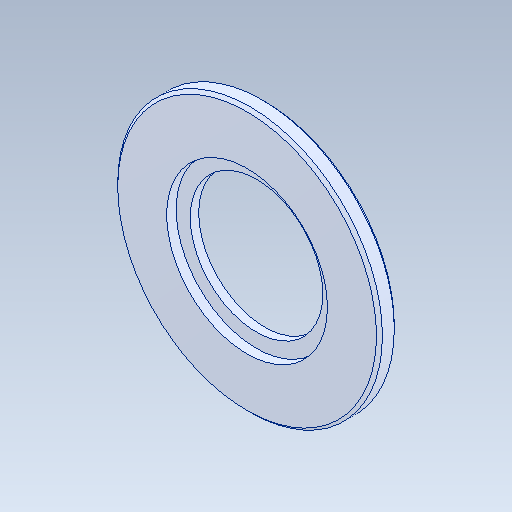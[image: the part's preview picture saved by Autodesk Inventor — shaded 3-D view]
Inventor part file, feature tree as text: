
AUTODESK INVENTOR PART (.ipt)
format: ipt  version: 2020 (Build 240168000, 168)  size: 107,520 bytes
history: native  units: in
note: dims shown in document units (in); Inventor stores cm internally (conversion verified against a paired STEP export)
features: chamfer x1
ambient origin geometry x8: Origin, YZ Plane, XZ Plane, XY Plane, X Axis, Y Axis, Z Axis, Center Point
bodies: Solid1 (feature_tree)
feature tree (1):
  chamfer  "Chamfer1"  [1 undecoded]
note: 1 required parameter value undecoded (feature->parameter linkage not recoverable at this tier; creation-order binding heuristic only, values carry confidence <= 0.55)
